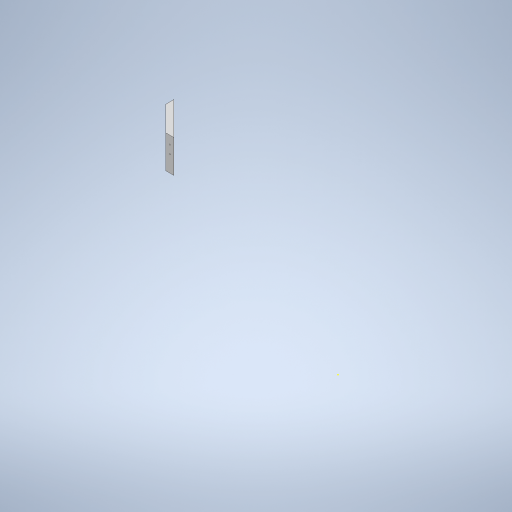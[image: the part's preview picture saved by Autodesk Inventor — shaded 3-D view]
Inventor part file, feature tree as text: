
AUTODESK INVENTOR PART (.ipt)
format: ipt  version: 2023 (Build 270158000, 158)  size: 360,960 bytes
history: native  units: in
note: dims shown in document units (in); Inventor stores cm internally (conversion verified against a paired STEP export)
features: other x8, hole x8, sketch x5, extrude x4, projected_geometry x1
ambient origin geometry x8: Origin, YZ Plane, XZ Plane, XY Plane, X Axis, Y Axis, Z Axis, Center Point
bodies: Solid1 (feature_tree)
feature tree (26):
  extrude  "Extrusion1"  Depth=54.0in
  extrude  "Extrusion2"  Depth=1.0in
  extrude  "Extrusion3"  Depth=16.0in
  other  "Work Axis1"
  other  "Work Axis2"
  other  "Work Axis3"
  other  "Work Axis4"
  other  "Work Point1"
  other  "Work Point2"
  other  "Work Point3"
  other  "Work Point4"
  hole  "Hole1"  [1 undecoded]
  hole  "Hole2"  [1 undecoded]
  hole  "Hole3"  [1 undecoded]
  hole  "Hole4"  [1 undecoded]
  hole  "Hole5"  [1 undecoded]
  hole  "Hole6"  [1 undecoded]
  hole  "Hole7"  [1 undecoded]
  hole  "Hole8"  [1 undecoded]
  sketch  "Sketch4"  dims[d6=8.0in d7=16.0in]
  extrude  "Extrusion4"  Depth=0.125in
  sketch  "Sketch1"  dims[d0=54.0in d1=54.0in]
  sketch  "Sketch2"  dims[d2=1.0in d3=1.0in]
  sketch  "Sketch3"  dims[d4=8.0in d5=16.0in]
  sketch  "Sketch5"  dims[d8=16.0in d9=8.0in d10=16.0in d11=8.0in d12=4.0in d13=4.0in d14=4.0in d15=4.0in d16=17.0in d17=17.0in d18=17.0in d19=17.0in d20=20.0in d21=1.0in d22=1.0in d23=1.0in d24=1.0in d25=45.0deg d26=2.5in d27=45.0deg d28=45.0deg d29=45.0deg d30=1.0in d31=1.0in d32=1.0in d33=1.0in d34=0.25in d35=0.25in d36=0.25in d37=0.25in d38=0.25in d39=0.25in d40=0.25in d41=0.25in d42=3.0in d43=0.0in d44=0.125in d45=0.125in d46=0.5in d47=1.0in d48=1.0in d49=0.5in d50=3.0in d51=0.0in d52=0.125in d53=0.125in d54=0.5in d55=0.5in d56=1.0in d57=1.0in d58=3.0in d59=0.0in d60=1.0in d61=1.0in d62=0.25in d63=0.75in d64=0.375in d65=0.25in d66=0.5635in d67=0.15in d68=0.0in d69=1.0in d70=1.0in d71=0.25in d72=0.75in d73=0.375in d74=0.25in d75=0.5635in d76=0.15in d77=0.0in d78=1.0in d79=1.0in d80=0.25in d81=0.75in d82=0.375in d83=0.25in d84=0.5635in d85=0.15in d86=0.0in d87=1.0in d88=1.0in d89=0.25in d90=0.75in d91=0.375in d92=0.25in d93=0.5635in d94=0.15in d95=0.0in d96=1.0in d97=1.0in d98=0.25in d99=0.75in d100=0.375in d101=0.25in d102=0.5635in d103=0.15in d104=0.0in d105=1.0in d106=1.0in d107=0.25in d108=0.75in d109=0.375in d110=0.25in d111=0.5635in d112=0.15in d113=0.0in d114=1.0in d115=1.0in d116=0.25in d117=0.75in d118=0.375in d119=0.25in d120=0.5635in d121=0.15in d122=0.0in d123=1.0in d124=1.0in d125=0.25in d126=0.75in d127=0.375in d128=0.25in d129=0.5635in d130=0.15in d131=0.0in d132=1.0in d133=0.0in]
  projected_geometry  "Projected Loop1"
note: 8 required parameter values undecoded (feature->parameter linkage not recoverable at this tier; creation-order binding heuristic only, values carry confidence <= 0.55)
